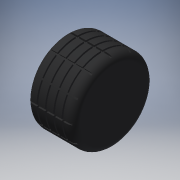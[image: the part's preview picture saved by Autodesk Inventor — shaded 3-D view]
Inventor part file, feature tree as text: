
AUTODESK INVENTOR PART (.ipt)
format: ipt  version: 2018 (Build 220112000, 112)  size: 561,152 bytes
history: native  units: in
note: dims shown in document units (in); Inventor stores cm internally (conversion verified against a paired STEP export)
features: sketch x3, plane x3, reference x3, other x3, extrude x2, revolve x1
ambient origin geometry x8: Origin, YZ Plane, XZ Plane, XY Plane, X Axis, Y Axis, Z Axis, Center Point
bodies: Solid1 (feature_tree)
feature tree (15):
  sketch  "Sketch1"  dims[d0=12.0in d1=24.0in d2=14.0in]
  plane  "Work Plane1"
  sketch  "Sketch2"  dims[d3=1.0in d4=0.0in d5=2.0in]
  plane  "Work Plane2"
  plane  "Work Plane3"
  extrude  "Extrusion1"  Depth=24.0in
  revolve  "Revolution1"  [1 undecoded]
  extrude  "Extrusion2"  Depth=0.5in
  reference  "Reference1"
  reference  "Reference2"
  reference  "Reference3"
  sketch  "Sketch3"  dims[d6=90.0deg d7=2.0in d8=0.5in d9=10.0in d10=0.5in d11=4.7244in d13=360.0deg d15=1.0in d16=0.0in]
  other  "<userpath>\Documents\Caleb School 2017-2018\GroupProject\HydraulicsCJE.iam"
  other  "HydraulicsCJE.iam"
  other  "Hydraulic ShaftCJE:1"
note: 1 required parameter value undecoded (feature->parameter linkage not recoverable at this tier; creation-order binding heuristic only, values carry confidence <= 0.55)
